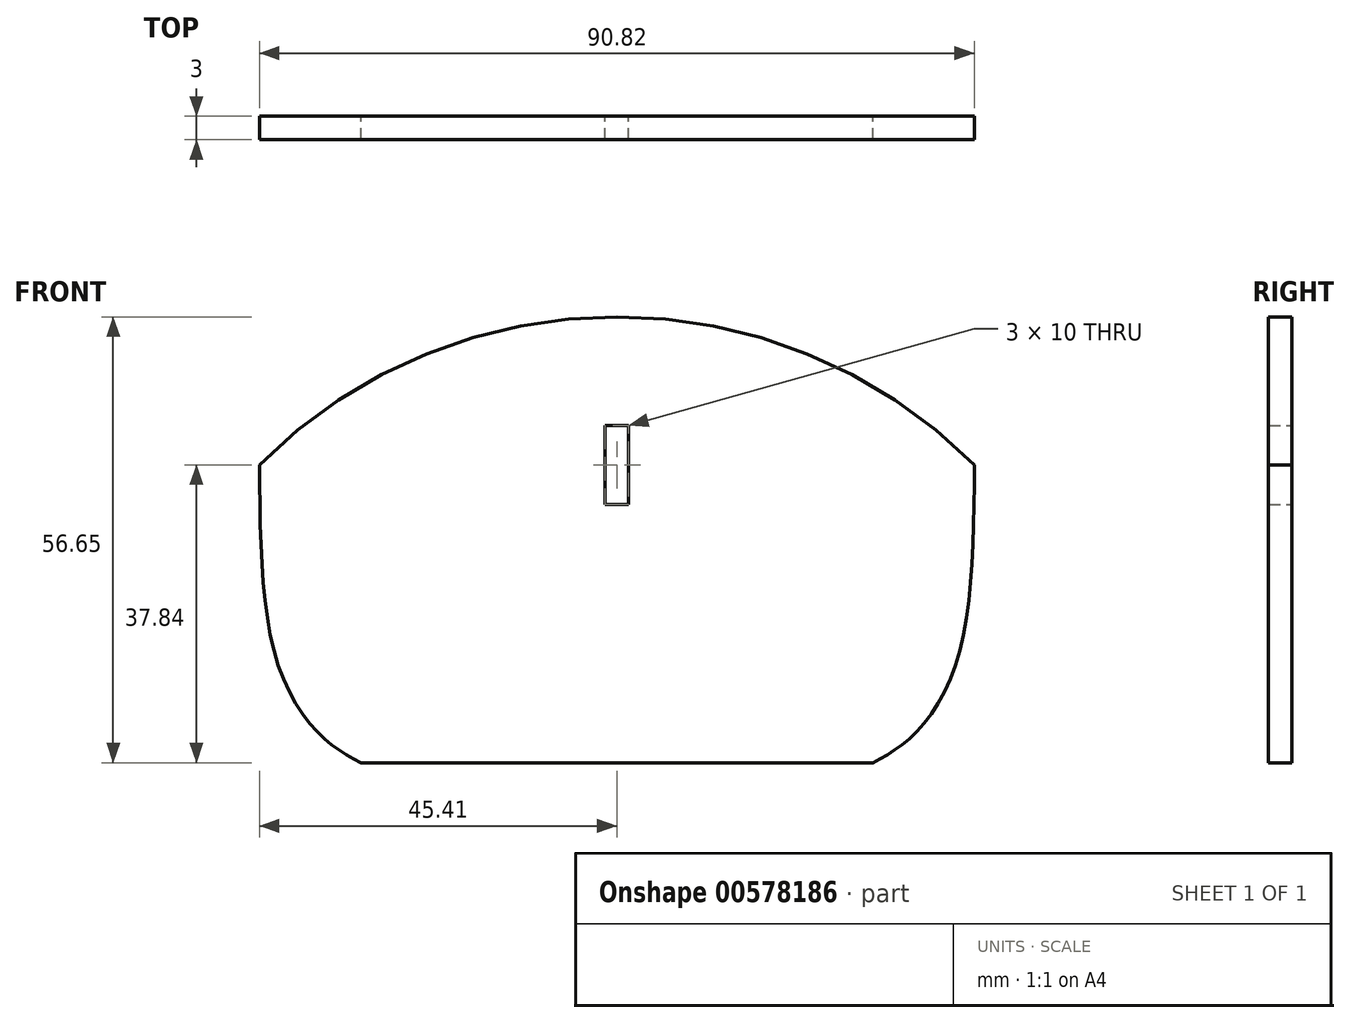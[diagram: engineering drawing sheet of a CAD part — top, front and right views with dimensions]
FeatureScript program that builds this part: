
annotation { "Feature Type Name" : "Feature", "Feature Type Description" : "" }
export const myFeature = defineFeature(function(context is Context, id is Id, definition is map)
    precondition{}
    {
        {
            var Q0;
            Q0=qCreatedBy(makeId("Front.planeOp"),FACE);
            var sketch = newSketch(context, id + "F0", { "sketchPlane" : qUnion([Q0])});
            skLineSegment(sketch, "E0", {"start": v(0, 0) * mm, "end": v(0, 396.99) * mm, "construction": true});
            skLineSegment(sketch, "E1", {"start": v(0, 0) * mm, "end": v(483.92, 0) * mm, "construction": true});
            skPoint(sketch, "E2.middle", {"position": v(0, -9.46) * mm});
            skArc(sketch, "E3", {"start": v(45.41, 0) * mm, "mid": v(0, 18.8) * mm, "end": v(-45.41, 0) * mm});
            skFitSpline(sketch, "E4", {"points": [v(-45.41, 0) * mm, v(-43.2, -24.83) * mm, v(-37.24, -34.71) * mm, v(-32.5, -37.84) * mm], "startDerivative": vector(0.5, -59.02) * mm, "endDerivative": vector(21.32, -11.38) * mm});
            skLineSegment(sketch, "E5", {"start": v(-32.5, -37.84) * mm, "end": v(0, -37.84) * mm});
            skLineSegment(sketch, "E6.MirrorCS", {"start": v(32.5, -37.84) * mm, "end": v(0, -37.84) * mm});
            skFitSpline(sketch, "E7.MirrorCS", {"points": [v(45.41, 0) * mm, v(43.2, -24.83) * mm, v(37.24, -34.71) * mm, v(32.5, -37.84) * mm], "startDerivative": vector(-0.5, -59.02) * mm, "endDerivative": vector(-21.32, -11.38) * mm});
            skLineSegment(sketch, "E8.bottom", {"start": v(1.5, -5) * mm, "end": v(-1.5, -5) * mm});
            skLineSegment(sketch, "E8.top", {"start": v(1.5, 5) * mm, "end": v(-1.5, 5) * mm});
            skLineSegment(sketch, "E8.left", {"start": v(1.5, -5) * mm, "end": v(1.5, 5) * mm});
            skLineSegment(sketch, "E8.right", {"start": v(-1.5, -5) * mm, "end": v(-1.5, 5) * mm});
            skPoint(sketch, "E8.middle", {"position": v(0, 0) * mm});
            skSolve(sketch);
        }
        {
            var Q0;
            Q0 = qSketchRegion(id + "F0", true);
            extrude(context, id + "F1", {"entities" : qUnion([Q0]), "endBound" : BoundingType.SYMMETRIC, "depth" : 3 * mm, "offsetDistance" : 25 * mm});
        }
    });
